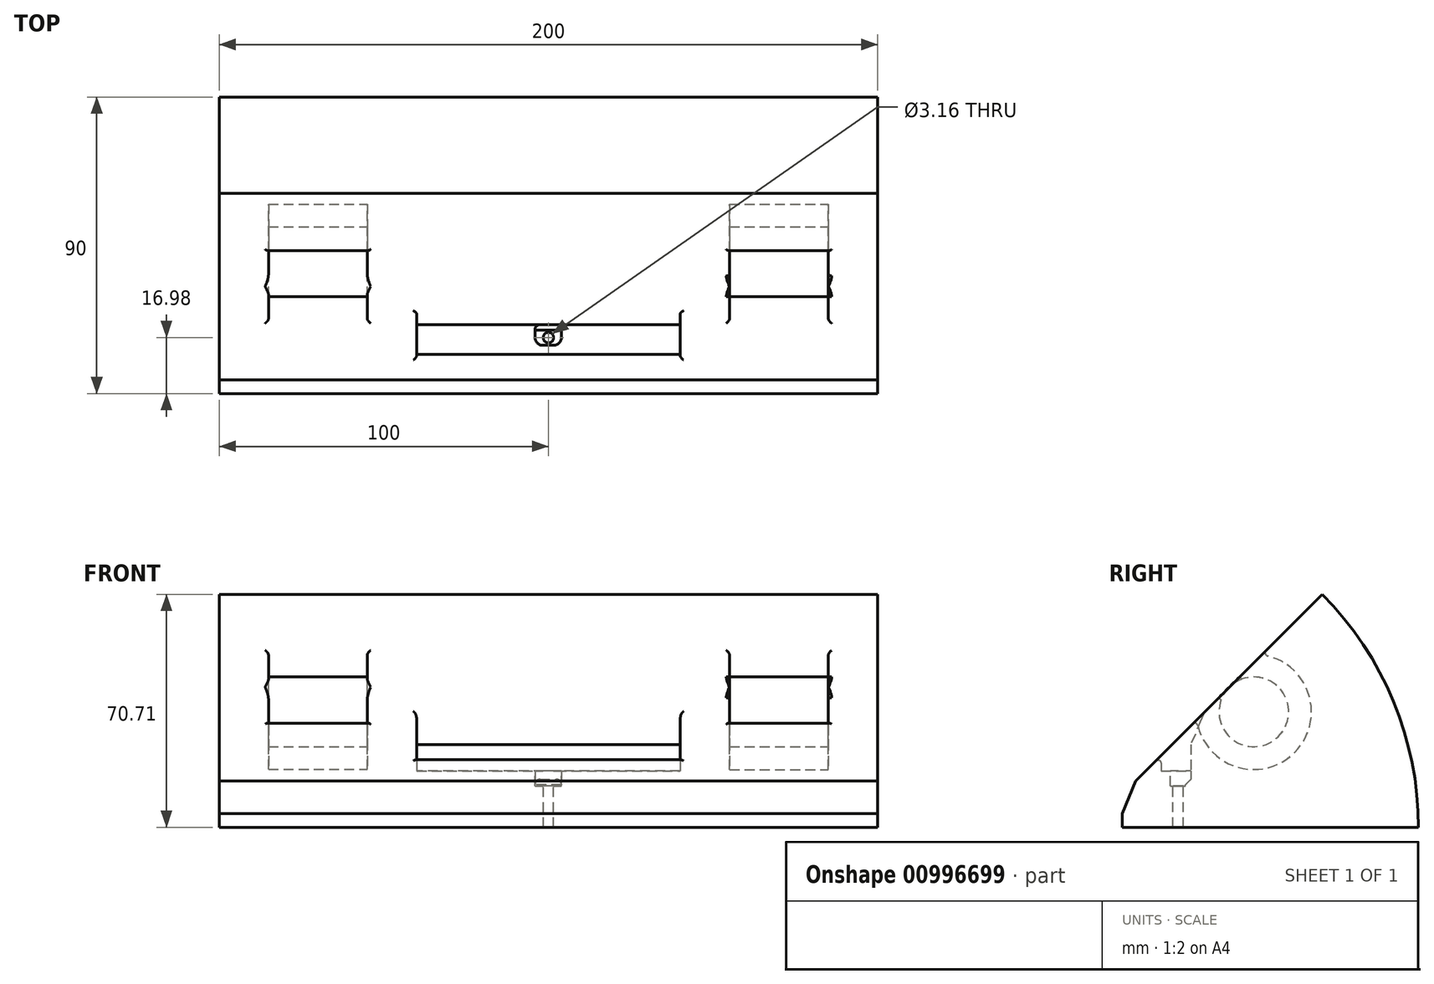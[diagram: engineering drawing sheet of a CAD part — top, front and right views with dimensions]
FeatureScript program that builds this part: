
annotation { "Feature Type Name" : "Feature", "Feature Type Description" : "" }
export const myFeature = defineFeature(function(context is Context, id is Id, definition is map)
    precondition{}
    {
        {
            var Q0;
            Q0=qCreatedBy(makeId("Top.planeOp"),FACE);
            var sketch = newSketch(context, id + "F0", { "sketchPlane" : qUnion([Q0])});
            skLineSegment(sketch, "E0.bottom", {"start": v(100, 50) * mm, "end": v(-100, 50) * mm});
            skLineSegment(sketch, "E0.top", {"start": v(100, -50) * mm, "end": v(-100, -50) * mm});
            skLineSegment(sketch, "E0.left", {"start": v(100, 50) * mm, "end": v(100, -50) * mm});
            skLineSegment(sketch, "E0.right", {"start": v(-100, 50) * mm, "end": v(-100, -50) * mm});
            skPoint(sketch, "E0.middle", {"position": v(0, 0) * mm});
            skSolve(sketch);
        }
        {
            var Q0;
            Q0=makeQuery(id+"F0.imprint","IMPRINT",FACE,{"disambiguationData":[TD([[makeQuery(id+"F0.imprint","IMPRINT",EDGE,{"derivedFrom":sQuery(id+"F0.wireOp",EDGE,"E0.bottom")}),1.0]])]});
            var Q1;
            Q1=sQuery(id+"F0.wireOp",EDGE,"E0.top");
            revolve(context, id + "F1", {"surfaceOperationType" : NewSurfaceOperationType.NEW, "entities" : qUnion([Q0]), "axis" : qUnion([Q1]), "revolveType" : RevolveType.ONE_DIRECTION, "oppositeDirection" : true, "angle" : 45 * degree});
        }
        {
            var Q0;
            Q0=qCreatedBy(makeId("Right.planeOp"),FACE);
            var sketch = newSketch(context, id + "F2", { "sketchPlane" : qUnion([Q0])});
            skLineSegment(sketch, "E1", {"start": v(0, 0) * mm, "end": v(-40, 0) * mm});
            skLineSegment(sketch, "E2", {"start": v(-40, 0) * mm, "end": v(-40, 19.1) * mm});
            skLineSegment(sketch, "E3", {"start": v(-40, 19.1) * mm, "end": v(-63.8, 19.1) * mm});
            skLineSegment(sketch, "E4", {"start": v(-63.8, 19.1) * mm, "end": v(-63.8, 0) * mm});
            skLineSegment(sketch, "E5", {"start": v(-63.8, 0) * mm, "end": v(-40, 0) * mm});
            skSolve(sketch);
        }
        {
            var Q0;
            Q0=makeQuery(id+"F2.imprint","IMPRINT",FACE,{"disambiguationData":[TD([[makeQuery(id+"F2.imprint","IMPRINT",EDGE,{"derivedFrom":sQuery(id+"F2.wireOp",EDGE,"E2")}),1.0]])]});
            extrude(context, id + "F3", {"entities" : qUnion([Q0]), "operationType" : NewBodyOperationType.REMOVE, "oppositeDirection" : true, "depth" : 114 * mm, "offsetDistance" : 25 * mm, "hasSecondDirection" : true, "secondDirectionOppositeDirection" : false, "secondDirectionDepth" : 151 * mm});
        }
        {
            var Q0;
            Q0=qCreatedBy(makeId("Top.planeOp"),FACE);
            cPlane(context, id + "F4", {"entities" : qUnion([Q0]), "cplaneType" : CPlaneType.OFFSET, "offset" : 17.1 * mm, "width" : 150 * mm, "height" : 150 * mm});
        }
        {
            var Q0;
            Q0=qCreatedBy(id+"F4.planeOp",FACE);
            var sketch = newSketch(context, id + "F5", { "sketchPlane" : qUnion([Q0])});
            skLineSegment(sketch, "E6", {"start": v(0, -28.12) * mm, "end": v(-40, -28.12) * mm});
            skLineSegment(sketch, "E7", {"start": v(40, -28.12) * mm, "end": v(0, -28.12) * mm});
            skLineSegment(sketch, "E8", {"start": v(40, -28.12) * mm, "end": v(40, -19.12) * mm});
            skLineSegment(sketch, "E9", {"start": v(0, -19.12) * mm, "end": v(40, -19.12) * mm});
            skLineSegment(sketch, "E10", {"start": v(-40, -19.12) * mm, "end": v(0, -19.12) * mm});
            skLineSegment(sketch, "E11", {"start": v(-40, -28.12) * mm, "end": v(-40, -19.12) * mm});
            skSolve(sketch);
        }
        {
            var Q0;
            Q0 = qSketchRegion(id + "F5", true);
            extrude(context, id + "F6", {"entities" : qUnion([Q0]), "operationType" : NewBodyOperationType.REMOVE, "depth" : 28.7 * mm, "offsetDistance" : 25 * mm});
        }
        {
            var Q0;
            Q0=qCreatedBy(makeId("Top.planeOp"),FACE);
            cPlane(context, id + "F7", {"entities" : qUnion([Q0]), "cplaneType" : CPlaneType.OFFSET, "offset" : 35.04 * mm, "width" : 150 * mm, "height" : 150 * mm});
        }
        {
            var Q0;
            Q0=qCreatedBy(makeId("Right.planeOp"),FACE);
            cPlane(context, id + "F8", {"entities" : qUnion([Q0]), "cplaneType" : CPlaneType.OFFSET, "offset" : 70 * mm, "oppositeDirection" : true, "width" : 150 * mm, "height" : 150 * mm});
        }
        {
            var Q0;
            Q0=qCreatedBy(id+"F8.planeOp",FACE);
            var sketch = newSketch(context, id + "F9", { "sketchPlane" : qUnion([Q0])});
            skCircle(sketch, "E12", {"center": v(0, 35.05) * mm, "radius": 10.57 * mm});
            skCircle(sketch, "E13", {"center": v(0, 35.05) * mm, "radius": 17.5 * mm});
            skSolve(sketch);
        }
        {
            var Q0;
            Q0=makeQuery(id+"F9.imprint","IMPRINT",FACE,{"disambiguationData":[TD([[makeQuery(id+"F9.imprint","IMPRINT",EDGE,{"derivedFrom":sQuery(id+"F9.wireOp",EDGE,"E12")}),-1.0]])]});
            extrude(context, id + "F10", {"entities" : qUnion([Q0]), "operationType" : NewBodyOperationType.REMOVE, "oppositeDirection" : true, "depth" : 15 * mm, "offsetDistance" : 25 * mm, "hasSecondDirection" : true, "secondDirectionOppositeDirection" : false, "secondDirectionDepth" : 15 * mm});
        }
        {
            var Q0;
            Q0=qCreatedBy(id+"F7.planeOp",FACE);
            var sketch = newSketch(context, id + "F11", { "sketchPlane" : qUnion([Q0])});
            skLineSegment(sketch, "E14", {"start": v(3.94, -23.08) * mm, "end": v(3.94, -20.78) * mm});
            skLineSegment(sketch, "E15", {"start": v(3.94, -23.08) * mm, "end": v(3.94, -25.38) * mm});
            skLineSegment(sketch, "E16", {"start": v(-0.06, -20.78) * mm, "end": v(-4.06, -20.78) * mm});
            skLineSegment(sketch, "E17", {"start": v(3.94, -20.78) * mm, "end": v(-0.06, -20.78) * mm});
            skLineSegment(sketch, "E18", {"start": v(-4.06, -23.08) * mm, "end": v(-4.06, -25.38) * mm});
            skLineSegment(sketch, "E19", {"start": v(-4.06, -23.08) * mm, "end": v(-4.06, -20.78) * mm});
            skLineSegment(sketch, "E20", {"start": v(-0.06, -25.38) * mm, "end": v(-4.06, -25.38) * mm});
            skLineSegment(sketch, "E21", {"start": v(3.94, -25.38) * mm, "end": v(-0.06, -25.38) * mm});
            skSolve(sketch);
        }
        {
            var Q0;
            Q0 = qSketchRegion(id + "F11", true);
            extrude(context, id + "F12", {"entities" : qUnion([Q0]), "operationType" : NewBodyOperationType.REMOVE, "oppositeDirection" : true, "depth" : 22.5 * mm, "offsetDistance" : 25 * mm});
        }
        {
            var Q0;
            Q0=makeQuery(id+"F3.boolean.opBoolean","INTERSECT",EDGE,{"derivedFrom":[makeQuery(id+"F1.opRevolve","CAP_FACE",FACE,{"disambiguationData":[OSD([sQuery(id+"F0.wireOp",EDGE,"E0.bottom"),sQuery(id+"F0.wireOp",EDGE,"E0.top"),sQuery(id+"F0.wireOp",EDGE,"E0.left"),sQuery(id+"F0.wireOp",EDGE,"E0.right")])],"isStart":false}),makeQuery(id+"F3.opExtrude","SWEPT_FACE",FACE,{"disambiguationData":[OSD([sQuery(id+"F2.wireOp",EDGE,"E2")])]})]});
            var Q1;
            Q1=makeQuery(id+"F6.boolean.opBoolean","INTERSECT",EDGE,{"derivedFrom":[makeQuery(id+"F1.opRevolve","CAP_FACE",FACE,{"disambiguationData":[OSD([sQuery(id+"F0.wireOp",EDGE,"E0.bottom"),sQuery(id+"F0.wireOp",EDGE,"E0.top"),sQuery(id+"F0.wireOp",EDGE,"E0.left"),sQuery(id+"F0.wireOp",EDGE,"E0.right")])],"isStart":false}),makeQuery(id+"F6.opExtrude","SWEPT_FACE",FACE,{"disambiguationData":[OSD([sQuery(id+"F5.wireOp",EDGE,"E9"),sQuery(id+"F5.wireOp",EDGE,"E10")])]})]});
            chamfer(context, id + "F13", {"entities" : qUnion([Q0, Q1]), "width" : 14 * mm, "tangentPropagation" : true});
        }
        {
            var Q0;
            Q0=makeQuery(id+"F12.boolean.opBoolean","INTERSECT",EDGE,{"derivedFrom":[makeQuery(id+"F6.boolean.opBoolean","COPY",FACE,{"derivedFrom":makeQuery(id+"F6.opExtrude","CAP_FACE",FACE,{"disambiguationData":[OSD([sQuery(id+"F5.wireOp",EDGE,"E6"),sQuery(id+"F5.wireOp",EDGE,"E7"),sQuery(id+"F5.wireOp",EDGE,"E8"),sQuery(id+"F5.wireOp",EDGE,"E9"),sQuery(id+"F5.wireOp",EDGE,"E10"),sQuery(id+"F5.wireOp",EDGE,"E11")])],"isStart":true})}),makeQuery(id+"F12.opExtrude","SWEPT_FACE",FACE,{"disambiguationData":[OSD([sQuery(id+"F11.wireOp",EDGE,"E16"),sQuery(id+"F11.wireOp",EDGE,"E17")])]})]});
            chamfer(context, id + "F14", {"entities" : qUnion([Q0]), "width" : 4.2 * mm, "tangentPropagation" : true});
        }
        {
            var Q0;
            Q0=makeQuery(id+"F12.boolean.opBoolean","COPY",EDGE,{"derivedFrom":makeQuery(id+"F12.opExtrude","SWEPT_EDGE",EDGE,{"disambiguationData":[OSD([sQuery(id+"F11.wireOp",EDGE,"E18"),sQuery(id+"F11.wireOp",EDGE,"E20")])]})});
            var Q1;
            Q1=makeQuery(id+"F12.boolean.opBoolean","COPY",EDGE,{"derivedFrom":makeQuery(id+"F12.opExtrude","SWEPT_EDGE",EDGE,{"disambiguationData":[OSD([sQuery(id+"F11.wireOp",EDGE,"E15"),sQuery(id+"F11.wireOp",EDGE,"E21")])]})});
            fillet(context, id + "F15", {"entities" : qUnion([Q0, Q1]), "radius" : 2.4 * mm, "tangentPropagation" : true, "allowEdgeOverflow" : false});
        }
        {
            var Q0;
            Q0=makeQuery(id+"F14.opChamfer","TWEAK_EDGE",EDGE,{"derivedFrom":[makeQuery(id+"F12.boolean.opBoolean","INTERSECT",VERTEX,{"derivedFrom":[makeQuery(id+"F6.boolean.opBoolean","COPY",FACE,{"derivedFrom":makeQuery(id+"F6.opExtrude","CAP_FACE",FACE,{"disambiguationData":[OSD([sQuery(id+"F5.wireOp",EDGE,"E6"),sQuery(id+"F5.wireOp",EDGE,"E7"),sQuery(id+"F5.wireOp",EDGE,"E8"),sQuery(id+"F5.wireOp",EDGE,"E9"),sQuery(id+"F5.wireOp",EDGE,"E10"),sQuery(id+"F5.wireOp",EDGE,"E11")])],"isStart":true})}),makeQuery(id+"F12.opExtrude","SWEPT_FACE",FACE,{"disambiguationData":[OSD([sQuery(id+"F11.wireOp",EDGE,"E16"),sQuery(id+"F11.wireOp",EDGE,"E17")])]}),makeQuery(id+"F12.opExtrude","SWEPT_FACE",FACE,{"disambiguationData":[OSD([sQuery(id+"F11.wireOp",EDGE,"E18"),sQuery(id+"F11.wireOp",EDGE,"E19")])]})]})]});
            var Q1;
            Q1=makeQuery(id+"F14.opChamfer","TWEAK_EDGE",EDGE,{"derivedFrom":[makeQuery(id+"F12.boolean.opBoolean","INTERSECT",VERTEX,{"derivedFrom":[makeQuery(id+"F6.boolean.opBoolean","COPY",FACE,{"derivedFrom":makeQuery(id+"F6.opExtrude","CAP_FACE",FACE,{"disambiguationData":[OSD([sQuery(id+"F5.wireOp",EDGE,"E6"),sQuery(id+"F5.wireOp",EDGE,"E7"),sQuery(id+"F5.wireOp",EDGE,"E8"),sQuery(id+"F5.wireOp",EDGE,"E9"),sQuery(id+"F5.wireOp",EDGE,"E10"),sQuery(id+"F5.wireOp",EDGE,"E11")])],"isStart":true})}),makeQuery(id+"F12.opExtrude","SWEPT_FACE",FACE,{"disambiguationData":[OSD([sQuery(id+"F11.wireOp",EDGE,"E14"),sQuery(id+"F11.wireOp",EDGE,"E15")])]}),makeQuery(id+"F12.opExtrude","SWEPT_FACE",FACE,{"disambiguationData":[OSD([sQuery(id+"F11.wireOp",EDGE,"E16"),sQuery(id+"F11.wireOp",EDGE,"E17")])]})]})]});
            fillet(context, id + "F16", {"entities" : qUnion([Q0, Q1]), "radius" : 1.5 * mm, "tangentPropagation" : true, "allowEdgeOverflow" : false});
        }
        {
            var Q0;
            Q0=qCreatedBy(id+"F7.planeOp",FACE);
            var sketch = newSketch(context, id + "F17", { "sketchPlane" : qUnion([Q0])});
            skCircle(sketch, "E22", {"center": v(0, -23.02) * mm, "radius": 1.58 * mm});
            skSolve(sketch);
        }
        {
            var Q0;
            Q0=makeQuery(id+"F17.imprint","IMPRINT",FACE,{"disambiguationData":[TD([[makeQuery(id+"F17.imprint","IMPRINT",EDGE,{"derivedFrom":sQuery(id+"F17.wireOp",EDGE,"E22")}),1.0]])]});
            extrude(context, id + "F18", {"entities" : qUnion([Q0]), "operationType" : NewBodyOperationType.REMOVE, "oppositeDirection" : true, "depth" : 100 * mm, "offsetDistance" : 25 * mm});
        }
        {
            var Q0;
            Q0=qCreatedBy(id+"F8.planeOp",FACE);
            cPlane(context, id + "F19", {"entities" : qUnion([Q0]), "cplaneType" : CPlaneType.OFFSET, "offset" : 140 * mm, "width" : 150 * mm, "height" : 150 * mm});
        }
        {
            var Q0;
            Q0=qCreatedBy(id+"F19.planeOp",FACE);
            var sketch = newSketch(context, id + "F20", { "sketchPlane" : qUnion([Q0])});
            skCircle(sketch, "E23", {"center": v(0, 35.04) * mm, "radius": 10.58 * mm});
            skCircle(sketch, "E24", {"center": v(0, 35.04) * mm, "radius": 17.5 * mm});
            skSolve(sketch);
        }
        {
            var Q0;
            Q0=makeQuery(id+"F20.imprint","IMPRINT",FACE,{"disambiguationData":[TD([[makeQuery(id+"F20.imprint","IMPRINT",EDGE,{"derivedFrom":sQuery(id+"F20.wireOp",EDGE,"E23")}),-1.0]])]});
            extrude(context, id + "F21", {"entities" : qUnion([Q0]), "operationType" : NewBodyOperationType.REMOVE, "oppositeDirection" : true, "depth" : 15 * mm, "offsetDistance" : 25 * mm, "hasSecondDirection" : true, "secondDirectionOppositeDirection" : false, "secondDirectionDepth" : 15 * mm});
        }
        {
            var Q0;
            Q0=makeQuery(id+"F6.boolean.opBoolean","INTERSECT",EDGE,{"derivedFrom":[makeQuery(id+"F1.opRevolve","CAP_FACE",FACE,{"disambiguationData":[OSD([sQuery(id+"F0.wireOp",EDGE,"E0.bottom"),sQuery(id+"F0.wireOp",EDGE,"E0.top"),sQuery(id+"F0.wireOp",EDGE,"E0.left"),sQuery(id+"F0.wireOp",EDGE,"E0.right")])],"isStart":false}),makeQuery(id+"F6.opExtrude","SWEPT_FACE",FACE,{"disambiguationData":[OSD([sQuery(id+"F5.wireOp",EDGE,"E11")])]})]});
            var Q1;
            {var subQ0=makeQuery(id+"F1.opRevolve","CAP_FACE",FACE,{"disambiguationData":[OSD([sQuery(id+"F0.wireOp",EDGE,"E0.bottom"),sQuery(id+"F0.wireOp",EDGE,"E0.top"),sQuery(id+"F0.wireOp",EDGE,"E0.left"),sQuery(id+"F0.wireOp",EDGE,"E0.right")])],"isStart":false});Q1=makeQuery(id+"F13.opChamfer","BLEND_EDGE",EDGE,{"blendedFrom":[makeQuery(id+"F6.boolean.opBoolean","INTERSECT",EDGE,{"derivedFrom":[subQ0,makeQuery(id+"F6.opExtrude","SWEPT_FACE",FACE,{"disambiguationData":[OSD([sQuery(id+"F5.wireOp",EDGE,"E9"),sQuery(id+"F5.wireOp",EDGE,"E10")])]})]}),subQ0],"blendedInto":[subQ0]});}
            var Q2;
            Q2=makeQuery(id+"F6.boolean.opBoolean","INTERSECT",EDGE,{"derivedFrom":[makeQuery(id+"F1.opRevolve","CAP_FACE",FACE,{"disambiguationData":[OSD([sQuery(id+"F0.wireOp",EDGE,"E0.bottom"),sQuery(id+"F0.wireOp",EDGE,"E0.top"),sQuery(id+"F0.wireOp",EDGE,"E0.left"),sQuery(id+"F0.wireOp",EDGE,"E0.right")])],"isStart":false}),makeQuery(id+"F6.opExtrude","SWEPT_FACE",FACE,{"disambiguationData":[OSD([sQuery(id+"F5.wireOp",EDGE,"E8")])]})]});
            var Q3;
            Q3=makeQuery(id+"F6.boolean.opBoolean","INTERSECT",EDGE,{"derivedFrom":[makeQuery(id+"F1.opRevolve","CAP_FACE",FACE,{"disambiguationData":[OSD([sQuery(id+"F0.wireOp",EDGE,"E0.bottom"),sQuery(id+"F0.wireOp",EDGE,"E0.top"),sQuery(id+"F0.wireOp",EDGE,"E0.left"),sQuery(id+"F0.wireOp",EDGE,"E0.right")])],"isStart":false}),makeQuery(id+"F6.opExtrude","SWEPT_FACE",FACE,{"disambiguationData":[OSD([sQuery(id+"F5.wireOp",EDGE,"E6"),sQuery(id+"F5.wireOp",EDGE,"E7")])]})]});
            var Q4;
            Q4=makeQuery(id+"F10.boolean.opBoolean","INTERSECT",EDGE,{"disambiguationData":[OD(1.0)],"derivedFrom":[makeQuery(id+"F1.opRevolve","CAP_FACE",FACE,{"disambiguationData":[OSD([sQuery(id+"F0.wireOp",EDGE,"E0.bottom"),sQuery(id+"F0.wireOp",EDGE,"E0.top"),sQuery(id+"F0.wireOp",EDGE,"E0.left"),sQuery(id+"F0.wireOp",EDGE,"E0.right")])],"isStart":false}),makeQuery(id+"F10.opExtrude","SWEPT_FACE",FACE,{"disambiguationData":[OSD([sQuery(id+"F9.wireOp",EDGE,"E13")])]})]});
            var Q5;
            Q5=makeQuery(id+"F10.boolean.opBoolean","INTERSECT",EDGE,{"disambiguationData":[OD(1.0)],"derivedFrom":[makeQuery(id+"F1.opRevolve","CAP_FACE",FACE,{"disambiguationData":[OSD([sQuery(id+"F0.wireOp",EDGE,"E0.bottom"),sQuery(id+"F0.wireOp",EDGE,"E0.top"),sQuery(id+"F0.wireOp",EDGE,"E0.left"),sQuery(id+"F0.wireOp",EDGE,"E0.right")])],"isStart":false}),makeQuery(id+"F10.opExtrude","CAP_FACE",FACE,{"disambiguationData":[OSD([sQuery(id+"F9.wireOp",EDGE,"E12"),sQuery(id+"F9.wireOp",EDGE,"E13")])],"isStart":false})]});
            var Q6;
            Q6=makeQuery(id+"F10.boolean.opBoolean","INTERSECT",EDGE,{"disambiguationData":[OD(0.0)],"derivedFrom":[makeQuery(id+"F1.opRevolve","CAP_FACE",FACE,{"disambiguationData":[OSD([sQuery(id+"F0.wireOp",EDGE,"E0.bottom"),sQuery(id+"F0.wireOp",EDGE,"E0.top"),sQuery(id+"F0.wireOp",EDGE,"E0.left"),sQuery(id+"F0.wireOp",EDGE,"E0.right")])],"isStart":false}),makeQuery(id+"F10.opExtrude","CAP_FACE",FACE,{"disambiguationData":[OSD([sQuery(id+"F9.wireOp",EDGE,"E12"),sQuery(id+"F9.wireOp",EDGE,"E13")])],"isStart":false})]});
            var Q7;
            Q7=makeQuery(id+"F10.boolean.opBoolean","INTERSECT",EDGE,{"disambiguationData":[OD(0.0)],"derivedFrom":[makeQuery(id+"F1.opRevolve","CAP_FACE",FACE,{"disambiguationData":[OSD([sQuery(id+"F0.wireOp",EDGE,"E0.bottom"),sQuery(id+"F0.wireOp",EDGE,"E0.top"),sQuery(id+"F0.wireOp",EDGE,"E0.left"),sQuery(id+"F0.wireOp",EDGE,"E0.right")])],"isStart":false}),makeQuery(id+"F10.opExtrude","SWEPT_FACE",FACE,{"disambiguationData":[OSD([sQuery(id+"F9.wireOp",EDGE,"E13")])]})]});
            var Q8;
            Q8=makeQuery(id+"F10.boolean.opBoolean","INTERSECT",EDGE,{"disambiguationData":[OD(0.0)],"derivedFrom":[makeQuery(id+"F1.opRevolve","CAP_FACE",FACE,{"disambiguationData":[OSD([sQuery(id+"F0.wireOp",EDGE,"E0.bottom"),sQuery(id+"F0.wireOp",EDGE,"E0.top"),sQuery(id+"F0.wireOp",EDGE,"E0.left"),sQuery(id+"F0.wireOp",EDGE,"E0.right")])],"isStart":false}),makeQuery(id+"F10.opExtrude","CAP_FACE",FACE,{"disambiguationData":[OSD([sQuery(id+"F9.wireOp",EDGE,"E12"),sQuery(id+"F9.wireOp",EDGE,"E13")])],"isStart":true})]});
            var Q9;
            Q9=makeQuery(id+"F10.boolean.opBoolean","INTERSECT",EDGE,{"disambiguationData":[OD(1.0)],"derivedFrom":[makeQuery(id+"F1.opRevolve","CAP_FACE",FACE,{"disambiguationData":[OSD([sQuery(id+"F0.wireOp",EDGE,"E0.bottom"),sQuery(id+"F0.wireOp",EDGE,"E0.top"),sQuery(id+"F0.wireOp",EDGE,"E0.left"),sQuery(id+"F0.wireOp",EDGE,"E0.right")])],"isStart":false}),makeQuery(id+"F10.opExtrude","CAP_FACE",FACE,{"disambiguationData":[OSD([sQuery(id+"F9.wireOp",EDGE,"E12"),sQuery(id+"F9.wireOp",EDGE,"E13")])],"isStart":true})]});
            var Q10;
            Q10=makeQuery(id+"F21.boolean.opBoolean","INTERSECT",EDGE,{"derivedFrom":[makeQuery(id+"F1.opRevolve","CAP_FACE",FACE,{"disambiguationData":[OSD([sQuery(id+"F0.wireOp",EDGE,"E0.bottom"),sQuery(id+"F0.wireOp",EDGE,"E0.top"),sQuery(id+"F0.wireOp",EDGE,"E0.left"),sQuery(id+"F0.wireOp",EDGE,"E0.right")])],"isStart":false}),makeQuery(id+"F21.opExtrude","CAP_FACE",FACE,{"disambiguationData":[OSD([sQuery(id+"F20.wireOp",EDGE,"E23"),sQuery(id+"F20.wireOp",EDGE,"E24")])],"isStart":true})]});
            var Q11;
            Q11=makeQuery(id+"F21.boolean.opBoolean","INTERSECT",EDGE,{"disambiguationData":[OD(1.0)],"derivedFrom":[makeQuery(id+"F1.opRevolve","CAP_FACE",FACE,{"disambiguationData":[OSD([sQuery(id+"F0.wireOp",EDGE,"E0.bottom"),sQuery(id+"F0.wireOp",EDGE,"E0.top"),sQuery(id+"F0.wireOp",EDGE,"E0.left"),sQuery(id+"F0.wireOp",EDGE,"E0.right")])],"isStart":false}),makeQuery(id+"F21.opExtrude","SWEPT_FACE",FACE,{"disambiguationData":[OSD([sQuery(id+"F20.wireOp",EDGE,"E24")])]})]});
            var Q12;
            Q12=makeQuery(id+"F21.boolean.opBoolean","INTERSECT",EDGE,{"derivedFrom":[makeQuery(id+"F1.opRevolve","CAP_FACE",FACE,{"disambiguationData":[OSD([sQuery(id+"F0.wireOp",EDGE,"E0.bottom"),sQuery(id+"F0.wireOp",EDGE,"E0.top"),sQuery(id+"F0.wireOp",EDGE,"E0.left"),sQuery(id+"F0.wireOp",EDGE,"E0.right")])],"isStart":false}),makeQuery(id+"F21.opExtrude","CAP_FACE",FACE,{"disambiguationData":[OSD([sQuery(id+"F20.wireOp",EDGE,"E23"),sQuery(id+"F20.wireOp",EDGE,"E24")])],"isStart":false})]});
            var Q13;
            Q13=makeQuery(id+"F21.boolean.opBoolean","INTERSECT",EDGE,{"disambiguationData":[OD(0.0)],"derivedFrom":[makeQuery(id+"F1.opRevolve","CAP_FACE",FACE,{"disambiguationData":[OSD([sQuery(id+"F0.wireOp",EDGE,"E0.bottom"),sQuery(id+"F0.wireOp",EDGE,"E0.top"),sQuery(id+"F0.wireOp",EDGE,"E0.left"),sQuery(id+"F0.wireOp",EDGE,"E0.right")])],"isStart":false}),makeQuery(id+"F21.opExtrude","SWEPT_FACE",FACE,{"disambiguationData":[OSD([sQuery(id+"F20.wireOp",EDGE,"E24")])]})]});
            fillet(context, id + "F22", {"entities" : qUnion([Q0, Q1, Q2, Q3, Q4, Q5, Q6, Q7, Q8, Q9, Q10, Q11, Q12, Q13]), "radius" : 1 * mm, "tangentPropagation" : true, "allowEdgeOverflow" : false});
        }
    });
